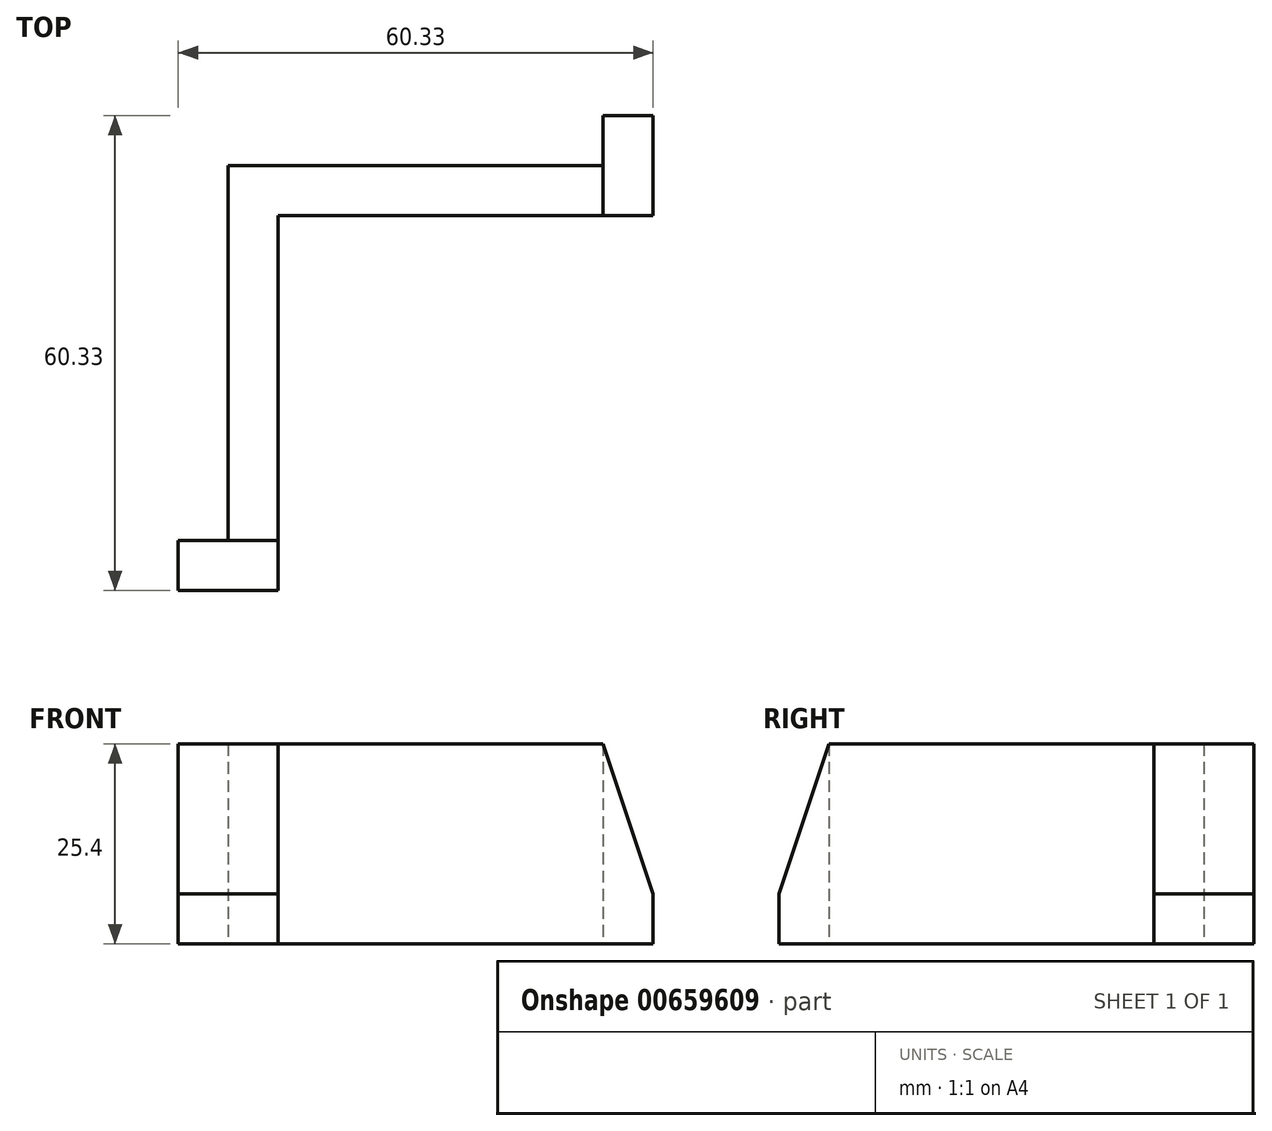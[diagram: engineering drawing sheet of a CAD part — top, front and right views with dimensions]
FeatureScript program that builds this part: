
annotation { "Feature Type Name" : "Feature", "Feature Type Description" : "" }
export const myFeature = defineFeature(function(context is Context, id is Id, definition is map)
    precondition{}
    {
        {
            var Q0;
            Q0=qCreatedBy(makeId("Top.planeOp"),FACE);
            var sketch = newSketch(context, id + "F0", { "sketchPlane" : qUnion([Q0])});
            skLineSegment(sketch, "E0.bottom", {"start": v(25.4, -25.4) * mm, "end": v(-25.4, -25.4) * mm});
            skLineSegment(sketch, "E0.top", {"start": v(25.4, 25.4) * mm, "end": v(-25.4, 25.4) * mm});
            skLineSegment(sketch, "E0.left", {"start": v(25.4, -25.4) * mm, "end": v(25.4, 25.4) * mm});
            skLineSegment(sketch, "E0.right", {"start": v(-25.4, -25.4) * mm, "end": v(-25.4, 25.4) * mm});
            skPoint(sketch, "E0.middle", {"position": v(0, 0) * mm});
            skLineSegment(sketch, "E1", {"start": v(22.23, 25.4) * mm, "end": v(22.23, 31.75) * mm});
            skLineSegment(sketch, "E2", {"start": v(22.23, 31.75) * mm, "end": v(-31.75, 31.75) * mm});
            skLineSegment(sketch, "E3", {"start": v(-31.75, 31.75) * mm, "end": v(-31.75, -22.23) * mm});
            skLineSegment(sketch, "E4", {"start": v(-31.75, -22.23) * mm, "end": v(-25.4, -22.23) * mm});
            skSolve(sketch);
        }
        {
            var Q0;
            {var subQ0=sQuery(id+"F0.wireOp",EDGE,"E1");Q0=makeQuery(id+"F0.imprint","IMPRINT",FACE,{"disambiguationData":[TD([[makeQuery(id+"F0.imprint","IMPRINT",EDGE,{"derivedFrom":subQ0}),1.0]])]});}
            extrude(context, id + "F1", {"entities" : qUnion([Q0]), "depth" : 25.4 * mm, "offsetDistance" : 25.4 * mm});
        }
        {
            var Q0;
            Q0=makeQuery(id+"F1.opExtrude","CAP_EDGE",EDGE,{"disambiguationData":[OSD([sQuery(id+"F0.wireOp",EDGE,"E4")])],"isStart":false});
            var Q1;
            Q1=makeQuery(id+"F1.opExtrude","CAP_EDGE",EDGE,{"disambiguationData":[OSD([sQuery(id+"F0.wireOp",EDGE,"E1")])],"isStart":false});
            chamfer(context, id + "F2", {"entities" : qUnion([Q0, Q1]), "chamferType" : ChamferType.TWO_OFFSETS, "width1" : 6.35 * mm, "oppositeDirection" : false, "width2" : 19.05 * mm, "tangentPropagation" : true});
        }
        {
            var Q0;
            Q0=makeQuery(id+"F1.opExtrude","SWEPT_FACE",FACE,{"disambiguationData":[OSD([sQuery(id+"F0.wireOp",EDGE,"E3")])]});
            var sketch = newSketch(context, id + "F3", { "sketchPlane" : qUnion([Q0])});
            skLineSegment(sketch, "E5", {"start": v(15.87, 25.4) * mm, "end": v(15.87, 0) * mm});
            skSolve(sketch);
        }
        {
            var Q0;
            Q0=makeQuery(id+"F1.opExtrude","SWEPT_FACE",FACE,{"disambiguationData":[OSD([sQuery(id+"F0.wireOp",EDGE,"E2")])]});
            var sketch = newSketch(context, id + "F4", { "sketchPlane" : qUnion([Q0])});
            skLineSegment(sketch, "E6", {"start": v(-15.88, 25.4) * mm, "end": v(-15.88, 0) * mm});
            skSolve(sketch);
        }
        {
            var Q0;
            {var subQ0=sQuery(id+"F4.wireOp",EDGE,"E6");Q0=makeQuery(id+"F4.imprint","IMPRINT",FACE,{"disambiguationData":[TD([[makeQuery(id+"F4.imprint","IMPRINT",EDGE,{"derivedFrom":subQ0}),-1.0]])]});}
            extrude(context, id + "F5", {"entities" : qUnion([Q0]), "operationType" : NewBodyOperationType.ADD, "depth" : 6.35 * mm, "offsetDistance" : 25.4 * mm});
        }
        {
            var Q0;
            {var subQ0=sQuery(id+"F3.wireOp",EDGE,"E5");Q0=makeQuery(id+"F3.imprint","IMPRINT",FACE,{"disambiguationData":[TD([[makeQuery(id+"F3.imprint","IMPRINT",EDGE,{"derivedFrom":subQ0}),1.0]])]});}
            extrude(context, id + "F6", {"entities" : qUnion([Q0]), "operationType" : NewBodyOperationType.ADD, "depth" : 6.35 * mm, "offsetDistance" : 25.4 * mm});
        }
    });
